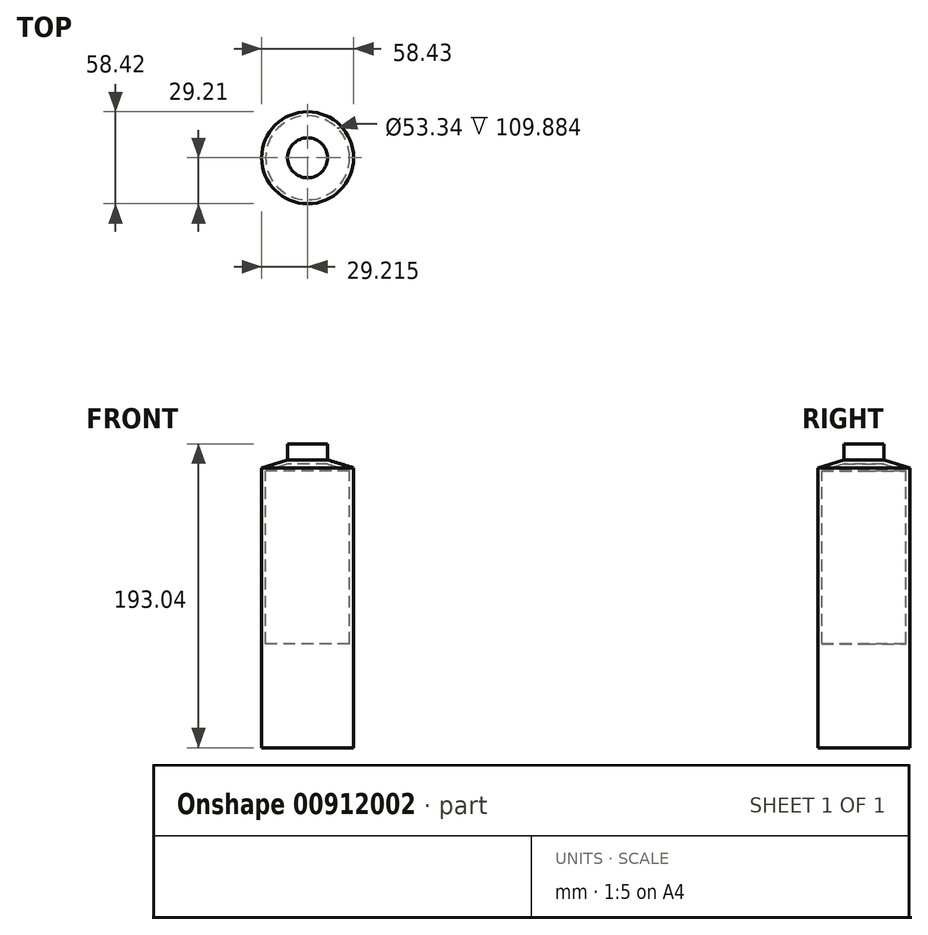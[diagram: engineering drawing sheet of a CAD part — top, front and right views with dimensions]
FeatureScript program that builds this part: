
annotation { "Feature Type Name" : "Feature", "Feature Type Description" : "" }
export const myFeature = defineFeature(function(context is Context, id is Id, definition is map)
    precondition{}
    {
        {
            var Q0;
            Q0=qCreatedBy(makeId("Front.planeOp"),FACE);
            var sketch = newSketch(context, id + "F0", { "sketchPlane" : qUnion([Q0])});
            skLineSegment(sketch, "E0.top", {"start": v(14.6, -88.9) * mm, "end": v(-14.6, -88.9) * mm});
            skLineSegment(sketch, "E0.left", {"start": v(14.6, 88.9) * mm, "end": v(14.6, -88.9) * mm});
            skLineSegment(sketch, "E0.right", {"start": v(-14.6, -22.86) * mm, "end": v(-14.6, -88.9) * mm, "construction": true});
            skPoint(sketch, "E0.middle", {"position": v(0, 0) * mm});
            skLineSegment(sketch, "E1.top", {"start": v(-14.6, 104.14) * mm, "end": v(-1.9, 104.14) * mm});
            skLineSegment(sketch, "E1.left", {"start": v(-14.6, 91.32) * mm, "end": v(-14.6, 104.14) * mm});
            skLineSegment(sketch, "E1.right", {"start": v(-1.9, 93.98) * mm, "end": v(-1.9, 104.14) * mm});
            skLineSegment(sketch, "E2", {"start": v(14.6, 88.9) * mm, "end": v(-1.9, 93.98) * mm});
            skPoint(sketch, "E0.bottom.start.orphan", {"position": v(-1.9, 92.48) * mm});
            skLineSegment(sketch, "E3", {"start": v(12.07, 87.02) * mm, "end": v(12.07, -22.86) * mm});
            skLineSegment(sketch, "E4", {"start": v(12.07, -22.86) * mm, "end": v(-14.6, -22.86) * mm});
            skLineSegment(sketch, "E5", {"start": v(-14.6, 104.14) * mm, "end": v(-14.6, 91.32) * mm});
            skLineSegment(sketch, "E6", {"start": v(-14.6, 91.32) * mm, "end": v(-1.9, 91.32) * mm});
            skLineSegment(sketch, "E7", {"start": v(-1.9, 91.32) * mm, "end": v(12.07, 87.02) * mm});
            skLineSegment(sketch, "E8.trimOffspring", {"start": v(-14.6, -22.86) * mm, "end": v(-14.6, -88.9) * mm});
            skPoint(sketch, "E9.orphan", {"position": v(-14.6, 88.9) * mm});
            skLineSegment(sketch, "E10", {"start": v(-14.6, 104.14) * mm, "end": v(-14.6, -88.9) * mm, "construction": true});
            skSolve(sketch);
        }
        {
            var Q0;
            Q0=makeQuery(id+"F0.imprint","IMPRINT",FACE,{"disambiguationData":[TD([[makeQuery(id+"F0.imprint","IMPRINT",EDGE,{"derivedFrom":sQuery(id+"F0.wireOp",EDGE,"E0.top")}),-1.0]])]});
            var Q1;
            Q1=sQuery(id+"F0.wireOp",EDGE,"E10");
            revolve(context, id + "F1", {"surfaceOperationType" : NewSurfaceOperationType.NEW, "entities" : qUnion([Q0]), "axis" : qUnion([Q1]), "revolveType" : RevolveType.FULL});
        }
    });
